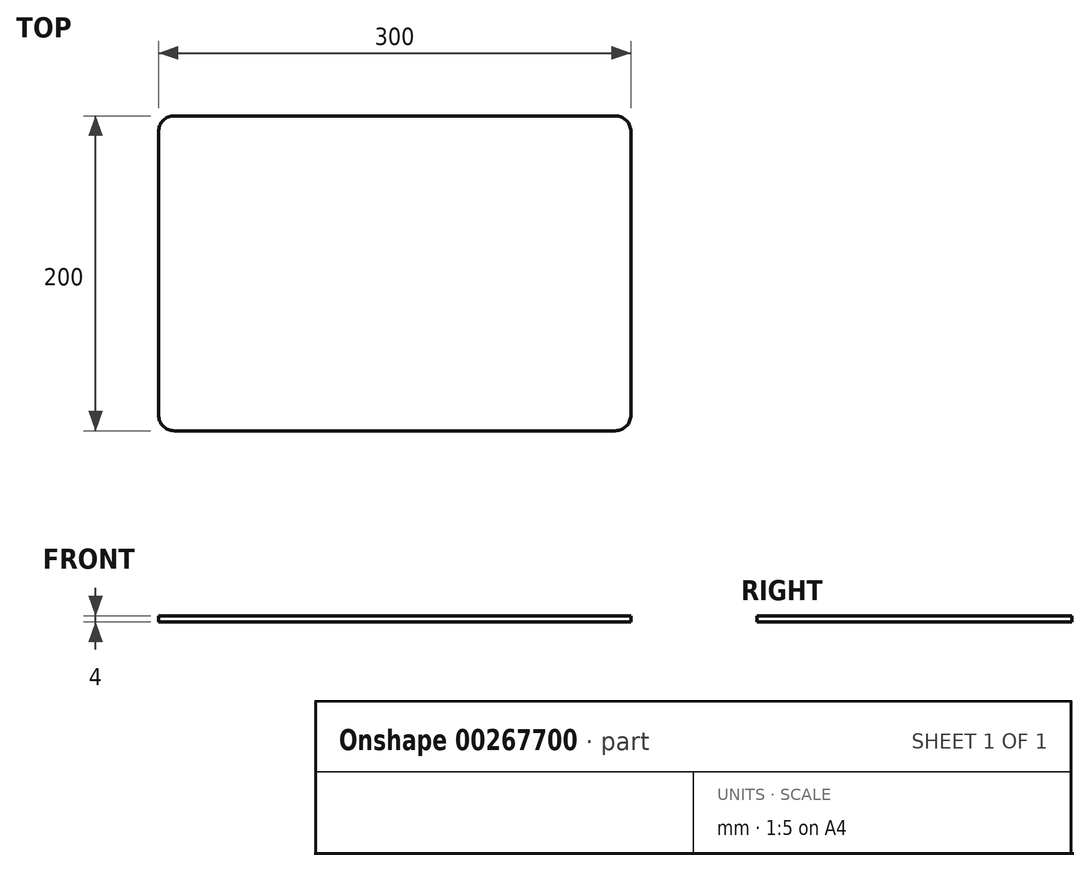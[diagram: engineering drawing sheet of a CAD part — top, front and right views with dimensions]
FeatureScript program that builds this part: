
annotation { "Feature Type Name" : "Feature", "Feature Type Description" : "" }
export const myFeature = defineFeature(function(context is Context, id is Id, definition is map)
    precondition{}
    {
        {
            var Q0;
            Q0=qCreatedBy(makeId("Top.planeOp"),FACE);
            var sketch = newSketch(context, id + "F0", { "sketchPlane" : qUnion([Q0])});
            skLineSegment(sketch, "E0.bottom", {"start": v(-140, 100) * mm, "end": v(140, 100) * mm});
            skLineSegment(sketch, "E0.top", {"start": v(-140, -100) * mm, "end": v(140, -100) * mm});
            skLineSegment(sketch, "E0.left", {"start": v(-150, 90) * mm, "end": v(-150, -90) * mm});
            skLineSegment(sketch, "E0.right", {"start": v(150, 90) * mm, "end": v(150, -90) * mm});
            skPoint(sketch, "E0.middle", {"position": v(0, 0) * mm});
            skPoint(sketch, "E1.visualSharp", {"position": v(-150, -100) * mm});
            skArc(sketch, "E1.filletArc", {"start": v(-150, -90) * mm, "mid": v(-147.07, -97.07) * mm, "end": v(-140, -100) * mm});
            skPoint(sketch, "E2.visualSharp", {"position": v(-150, 100) * mm});
            skArc(sketch, "E2.filletArc", {"start": v(-140, 100) * mm, "mid": v(-147.07, 97.07) * mm, "end": v(-150, 90) * mm});
            skPoint(sketch, "E3.visualSharp", {"position": v(150, 100) * mm});
            skArc(sketch, "E3.filletArc", {"start": v(150, 90) * mm, "mid": v(147.07, 97.07) * mm, "end": v(140, 100) * mm});
            skPoint(sketch, "E4.visualSharp", {"position": v(150, -100) * mm});
            skArc(sketch, "E4.filletArc", {"start": v(140, -100) * mm, "mid": v(147.07, -97.07) * mm, "end": v(150, -90) * mm});
            skSolve(sketch);
        }
        {
            var Q0;
            Q0=qSketchRegion(id+"F0",true);
            extrude(context, id + "F1", {"entities" : qUnion([Q0]), "oppositeDirection" : true, "depth" : 4 * mm});
        }
    });
